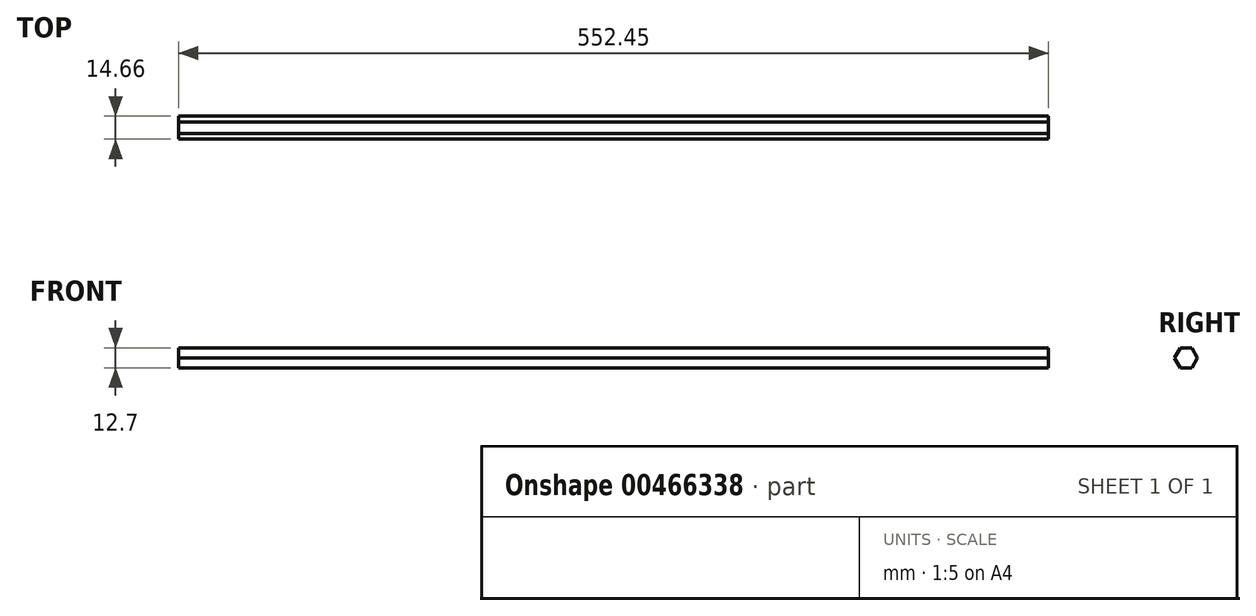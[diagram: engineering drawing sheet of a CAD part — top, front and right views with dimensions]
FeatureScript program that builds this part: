
annotation { "Feature Type Name" : "Feature", "Feature Type Description" : "" }
export const myFeature = defineFeature(function(context is Context, id is Id, definition is map)
    precondition{}
    {
        {
            var Q0;
            Q0=qCreatedBy(makeId("Right.planeOp"),FACE);
            var sketch = newSketch(context, id + "F0", { "sketchPlane" : qUnion([Q0])});
            skCircle(sketch, "E0.cCircle", {"center": v(0, 0) * mm, "radius": 6.35 * mm, "construction": true});
            skLineSegment(sketch, "E0.0", {"start": v(-7.33, 0) * mm, "end": v(-3.67, 6.35) * mm});
            skLineSegment(sketch, "E0.1", {"start": v(-3.67, 6.35) * mm, "end": v(3.66, 6.35) * mm});
            skLineSegment(sketch, "E0.2", {"start": v(3.66, 6.35) * mm, "end": v(7.33, 0) * mm});
            skLineSegment(sketch, "E0.3", {"start": v(7.33, 0) * mm, "end": v(3.67, -6.35) * mm});
            skLineSegment(sketch, "E0.4", {"start": v(3.67, -6.35) * mm, "end": v(-3.66, -6.35) * mm});
            skLineSegment(sketch, "E0.5", {"start": v(-3.66, -6.35) * mm, "end": v(-7.33, 0) * mm});
            skPoint(sketch, "E0.0.midPoint", {"position": v(-5.5, 3.17) * mm});
            skSolve(sketch);
        }
        {
            var Q0;
            Q0=makeQuery(id+"F0.imprint","IMPRINT",FACE,{"disambiguationData":[TD([[makeQuery(id+"F0.imprint","IMPRINT",EDGE,{"derivedFrom":sQuery(id+"F0.wireOp",EDGE,"E0.0")}),-1.0]])]});
            extrude(context, id + "F1", {"entities" : qUnion([Q0]), "depth" : 552.45 * mm});
        }
    });
